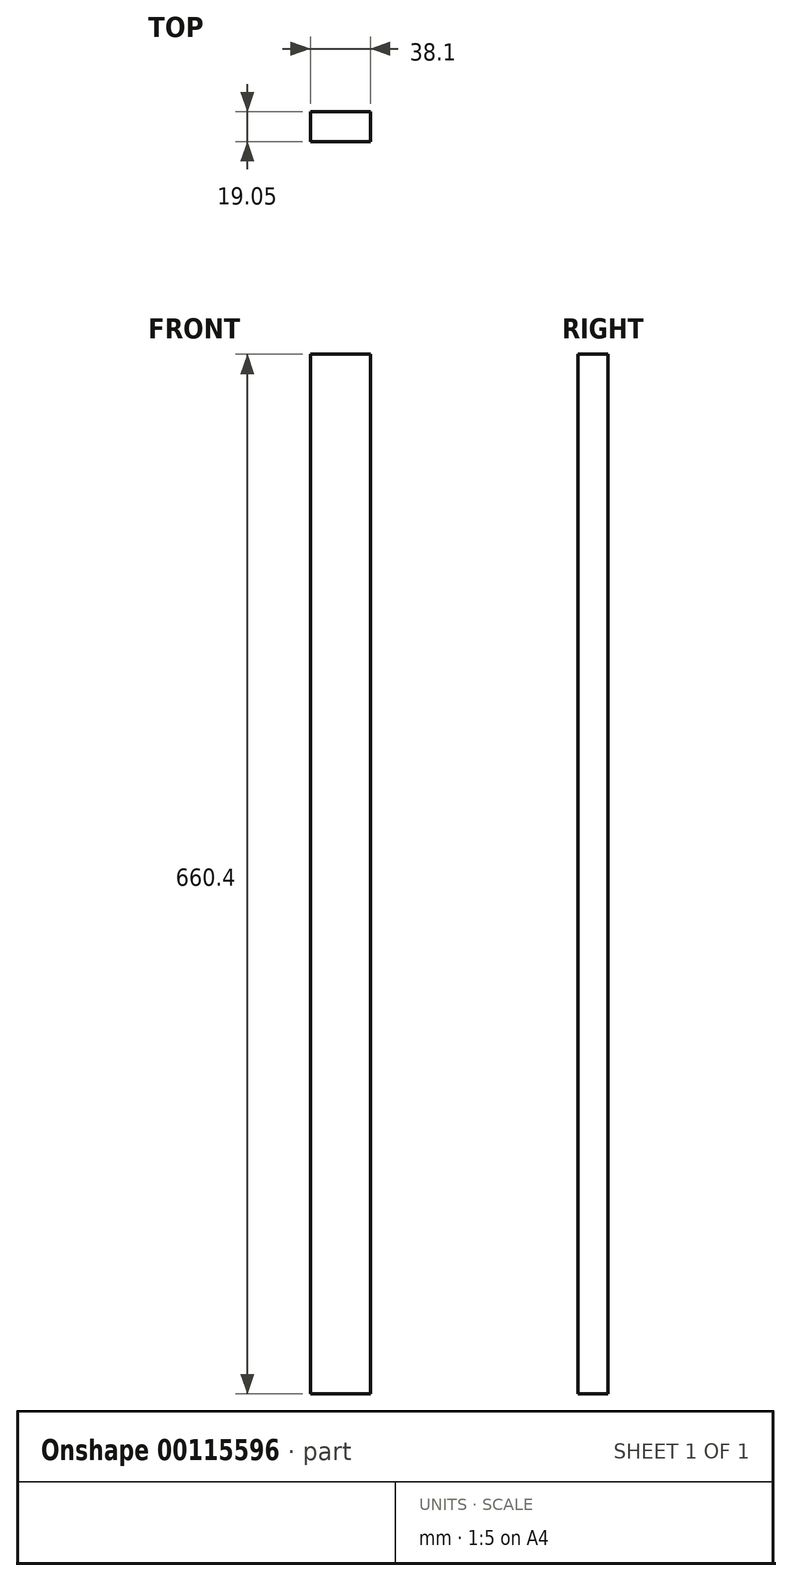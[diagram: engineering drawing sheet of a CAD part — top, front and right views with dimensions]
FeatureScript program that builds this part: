
annotation { "Feature Type Name" : "Feature", "Feature Type Description" : "" }
export const myFeature = defineFeature(function(context is Context, id is Id, definition is map)
    precondition{}
    {
        {
            var Q0;
            Q0=qCreatedBy(makeId("Front.planeOp"),FACE);
            var sketch = newSketch(context, id + "F0", { "sketchPlane" : qUnion([Q0])});
            skLineSegment(sketch, "E0.bottom", {"start": v(-19.05, 330.2) * mm, "end": v(19.05, 330.2) * mm});
            skLineSegment(sketch, "E0.top", {"start": v(-19.05, -330.2) * mm, "end": v(19.05, -330.2) * mm});
            skLineSegment(sketch, "E0.left", {"start": v(-19.05, 330.2) * mm, "end": v(-19.05, -330.2) * mm});
            skLineSegment(sketch, "E0.right", {"start": v(19.05, 330.2) * mm, "end": v(19.05, -330.2) * mm});
            skPoint(sketch, "E0.middle", {"position": v(0, 0) * mm});
            skSolve(sketch);
        }
        {
            var Q0;
            Q0=makeQuery(id+"F0.imprint","IMPRINT",FACE,{"disambiguationData":[TD([[makeQuery(id+"F0.imprint","IMPRINT",EDGE,{"derivedFrom":sQuery(id+"F0.wireOp",EDGE,"E0.bottom")}),-1.0]])]});
            extrude(context, id + "F1", {"entities" : qUnion([Q0]), "depth" : 19.05 * mm});
        }
    });
